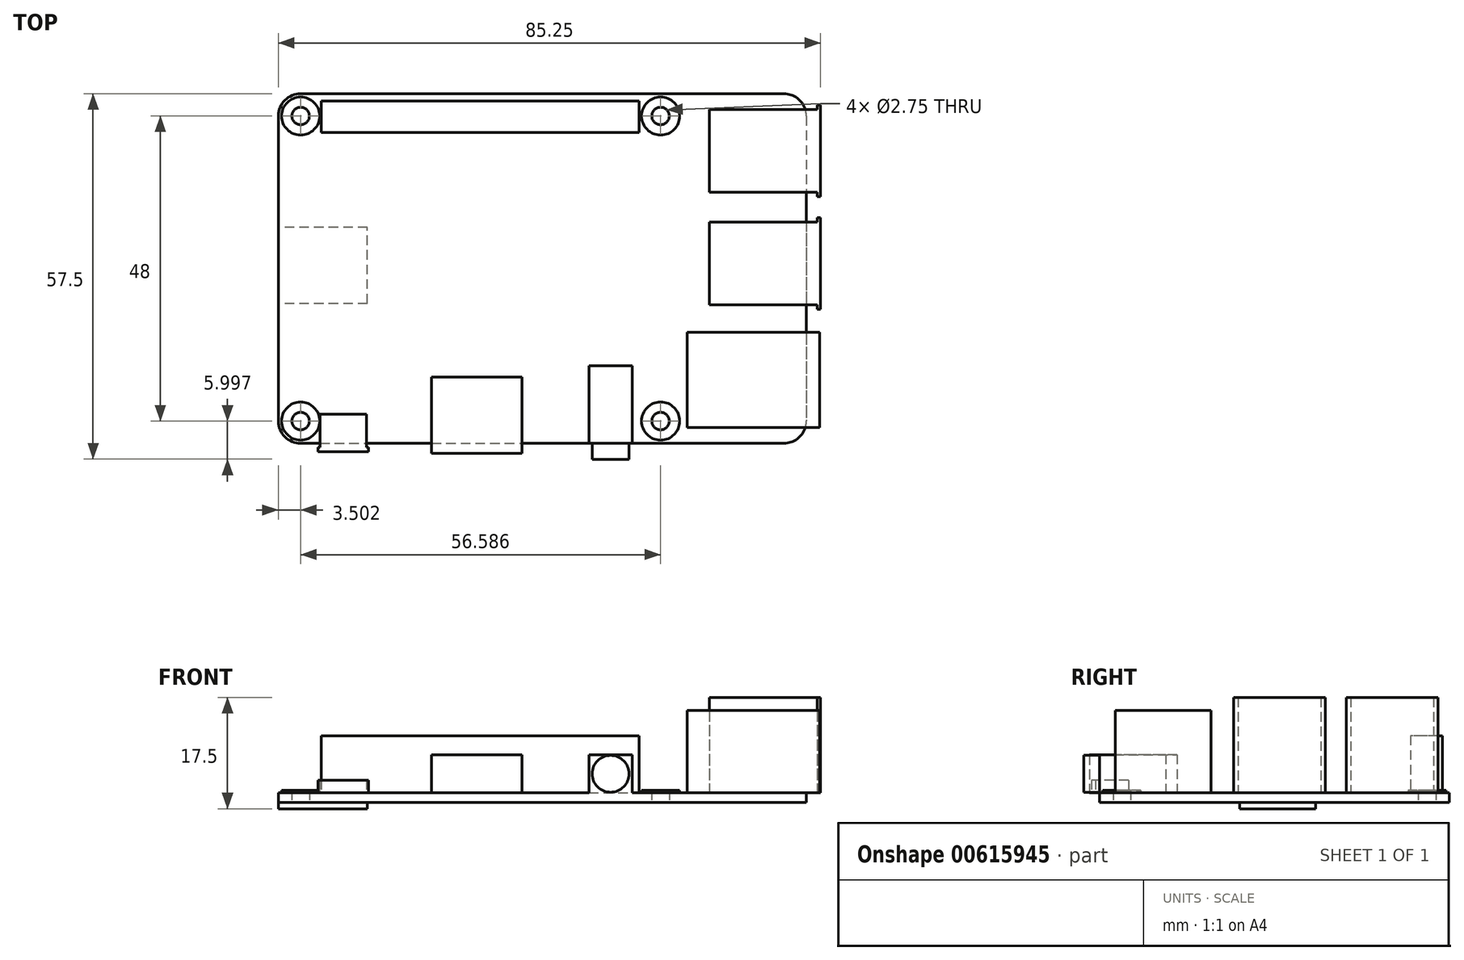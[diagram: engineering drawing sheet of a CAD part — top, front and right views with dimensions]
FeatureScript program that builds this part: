
annotation { "Feature Type Name" : "Feature", "Feature Type Description" : "" }
export const myFeature = defineFeature(function(context is Context, id is Id, definition is map)
    precondition{}
    {
        {
            var Q0;
            Q0=qCreatedBy(makeId("Top.planeOp"),FACE);
            var sketch = newSketch(context, id + "F0", { "sketchPlane" : qUnion([Q0])});
            skLineSegment(sketch, "E0.bottom", {"start": v(20.88, 73.76) * mm, "end": v(96.88, 73.76) * mm});
            skLineSegment(sketch, "E0.top", {"start": v(20.88, 18.76) * mm, "end": v(96.88, 18.76) * mm});
            skLineSegment(sketch, "E0.left", {"start": v(17.38, 70.26) * mm, "end": v(17.38, 22.26) * mm});
            skLineSegment(sketch, "E0.right", {"start": v(100.38, 70.26) * mm, "end": v(100.38, 22.26) * mm});
            skPoint(sketch, "E1.visualSharp", {"position": v(17.38, 73.76) * mm});
            skArc(sketch, "E1.filletArc", {"start": v(20.88, 73.76) * mm, "mid": v(18.4, 72.73) * mm, "end": v(17.38, 70.26) * mm});
            skPoint(sketch, "E2.visualSharp", {"position": v(100.38, 73.76) * mm});
            skArc(sketch, "E2.filletArc", {"start": v(100.38, 70.26) * mm, "mid": v(99.36, 72.73) * mm, "end": v(96.88, 73.76) * mm});
            skPoint(sketch, "E3.visualSharp", {"position": v(100.38, 18.76) * mm});
            skArc(sketch, "E3.filletArc", {"start": v(96.88, 18.76) * mm, "mid": v(99.36, 19.78) * mm, "end": v(100.38, 22.26) * mm});
            skPoint(sketch, "E4.visualSharp", {"position": v(17.38, 18.76) * mm});
            skArc(sketch, "E4.filletArc", {"start": v(17.38, 22.26) * mm, "mid": v(18.4, 19.78) * mm, "end": v(20.88, 18.76) * mm});
            skSolve(sketch);
        }
        {
            var Q0;
            Q0=makeQuery(id+"F0.imprint","IMPRINT",FACE,{"disambiguationData":[TD([[makeQuery(id+"F0.imprint","IMPRINT",EDGE,{"derivedFrom":sQuery(id+"F0.wireOp",EDGE,"E0.bottom")}),-1.0]])]});
            extrude(context, id + "F1", {"entities" : qUnion([Q0]), "depth" : 1.5 * mm, "offsetDistance" : 25 * mm, "symmetric" : true});
        }
        {
            var Q0;
            Q0=makeQuery(id+"F1.opExtrude","CAP_FACE",FACE,{"disambiguationData":[OSD([sQuery(id+"F0.wireOp",EDGE,"E0.bottom"),sQuery(id+"F0.wireOp",EDGE,"E0.top"),sQuery(id+"F0.wireOp",EDGE,"E0.left"),sQuery(id+"F0.wireOp",EDGE,"E0.right"),sQuery(id+"F0.wireOp",EDGE,"E1.filletArc"),sQuery(id+"F0.wireOp",EDGE,"E2.filletArc"),sQuery(id+"F0.wireOp",EDGE,"E3.filletArc"),sQuery(id+"F0.wireOp",EDGE,"E4.filletArc")])],"isStart":false});
            var sketch = newSketch(context, id + "F2", { "sketchPlane" : qUnion([Q0])});
            skLineSegment(sketch, "E5.bottom", {"start": v(85.13, 71.26) * mm, "end": v(102.13, 71.26) * mm});
            skLineSegment(sketch, "E5.top", {"start": v(85.13, 58.26) * mm, "end": v(102.13, 58.26) * mm});
            skLineSegment(sketch, "E5.left", {"start": v(85.13, 71.26) * mm, "end": v(85.13, 58.26) * mm});
            skLineSegment(sketch, "E6", {"start": v(102.13, 71.26) * mm, "end": v(102.13, 71.96) * mm});
            skLineSegment(sketch, "E7", {"start": v(102.13, 71.96) * mm, "end": v(102.63, 71.96) * mm});
            skLineSegment(sketch, "E8", {"start": v(102.13, 58.26) * mm, "end": v(102.13, 57.56) * mm});
            skLineSegment(sketch, "E9", {"start": v(102.13, 57.56) * mm, "end": v(102.63, 57.56) * mm});
            skLineSegment(sketch, "E10", {"start": v(102.63, 57.56) * mm, "end": v(102.63, 71.96) * mm});
            skLineSegment(sketch, "E11.bottom", {"start": v(85.13, 53.55) * mm, "end": v(102.12, 53.55) * mm});
            skLineSegment(sketch, "E11.top", {"start": v(85.13, 40.55) * mm, "end": v(102.13, 40.55) * mm});
            skLineSegment(sketch, "E11.left", {"start": v(85.13, 53.55) * mm, "end": v(85.13, 40.55) * mm});
            skLineSegment(sketch, "E12", {"start": v(102.12, 53.55) * mm, "end": v(102.12, 54.25) * mm});
            skLineSegment(sketch, "E13", {"start": v(102.12, 54.25) * mm, "end": v(102.63, 54.25) * mm});
            skLineSegment(sketch, "E14", {"start": v(102.63, 54.25) * mm, "end": v(102.63, 39.85) * mm});
            skLineSegment(sketch, "E15", {"start": v(102.63, 39.85) * mm, "end": v(102.13, 39.85) * mm});
            skLineSegment(sketch, "E16", {"start": v(102.13, 39.85) * mm, "end": v(102.13, 40.55) * mm});
            skLineSegment(sketch, "E17.bottom", {"start": v(85.13, 36.26) * mm, "end": v(102.5, 36.26) * mm});
            skLineSegment(sketch, "E17.top", {"start": v(85.13, 21.26) * mm, "end": v(102.5, 21.26) * mm});
            skLineSegment(sketch, "E17.right", {"start": v(102.5, 36.26) * mm, "end": v(102.5, 21.26) * mm});
            skLineSegment(sketch, "E18", {"start": v(85.13, 36.26) * mm, "end": v(81.63, 36.26) * mm});
            skLineSegment(sketch, "E19", {"start": v(85.13, 21.26) * mm, "end": v(81.63, 21.26) * mm});
            skLineSegment(sketch, "E20", {"start": v(81.63, 36.26) * mm, "end": v(81.63, 21.26) * mm});
            skSolve(sketch);
        }
        {
            var Q0;
            {var subQ5=sQuery(id+"F2.wireOp",EDGE,"E5.left");Q0=makeQuery(id+"F2.imprint","IMPRINT",FACE,{"disambiguationData":[TD([[makeQuery(id+"F2.imprint","IMPRINT",EDGE,{"derivedFrom":subQ5}),1.0]])]});}
            var Q1;
            {var subQ0=sQuery(id+"F2.wireOp",EDGE,"E6");Q1=makeQuery(id+"F2.imprint","IMPRINT",FACE,{"disambiguationData":[TD([[makeQuery(id+"F2.imprint","IMPRINT",EDGE,{"derivedFrom":subQ0}),-1.0]])]});}
            var Q2;
            {var subQ0=sQuery(id+"F2.wireOp",EDGE,"E12");Q2=makeQuery(id+"F2.imprint","IMPRINT",FACE,{"disambiguationData":[TD([[makeQuery(id+"F2.imprint","IMPRINT",EDGE,{"derivedFrom":subQ0}),-1.0]])]});}
            var Q3;
            {var subQ0=sQuery(id+"F2.wireOp",EDGE,"E11.left");Q3=makeQuery(id+"F2.imprint","IMPRINT",FACE,{"disambiguationData":[TD([[makeQuery(id+"F2.imprint","IMPRINT",EDGE,{"derivedFrom":subQ0}),1.0]])]});}
            var Q4;
            {var subQ4=sQuery(id+"F2.wireOp",EDGE,"E18");Q4=makeQuery(id+"F2.imprint","IMPRINT",FACE,{"disambiguationData":[TD([[makeQuery(id+"F2.imprint","IMPRINT",EDGE,{"derivedFrom":subQ4}),1.0]])]});}
            var Q5;
            {var subQ5=sQuery(id+"F2.wireOp",EDGE,"E17.right");Q5=makeQuery(id+"F2.imprint","IMPRINT",FACE,{"disambiguationData":[TD([[makeQuery(id+"F2.imprint","IMPRINT",EDGE,{"derivedFrom":subQ5}),-1.0]])]});}
            extrude(context, id + "F3", {"entities" : qUnion([Q0, Q1, Q2, Q3, Q4, Q5]), "operationType" : NewBodyOperationType.ADD, "depth" : 15 * mm, "offsetDistance" : 25 * mm});
        }
        {
            var Q0;
            Q0=makeQuery(id+"F3.opExtrude","CAP_FACE",FACE,{"disambiguationData":[OSD([sQuery(id+"F2.wireOp",EDGE,"E17.bottom"),sQuery(id+"F2.wireOp",EDGE,"E17.top"),sQuery(id+"F2.wireOp",EDGE,"E17.right"),sQuery(id+"F2.wireOp",EDGE,"E18"),sQuery(id+"F2.wireOp",EDGE,"E19"),sQuery(id+"F2.wireOp",EDGE,"E20")])],"isStart":false});
            extrude(context, id + "F4", {"entities" : qUnion([Q0]), "operationType" : NewBodyOperationType.REMOVE, "oppositeDirection" : true, "depth" : 2 * mm, "offsetDistance" : 25 * mm});
        }
        {
            var Q0;
            Q0=makeQuery(id+"F1.opExtrude","CAP_FACE",FACE,{"disambiguationData":[OSD([sQuery(id+"F0.wireOp",EDGE,"E0.bottom"),sQuery(id+"F0.wireOp",EDGE,"E0.top"),sQuery(id+"F0.wireOp",EDGE,"E0.left"),sQuery(id+"F0.wireOp",EDGE,"E0.right"),sQuery(id+"F0.wireOp",EDGE,"E1.filletArc"),sQuery(id+"F0.wireOp",EDGE,"E2.filletArc"),sQuery(id+"F0.wireOp",EDGE,"E3.filletArc"),sQuery(id+"F0.wireOp",EDGE,"E4.filletArc")])],"isStart":false});
            var sketch = newSketch(context, id + "F5", { "sketchPlane" : qUnion([Q0])});
            skLineSegment(sketch, "E21.bottom", {"start": v(24.1, 72.64) * mm, "end": v(74.1, 72.64) * mm});
            skLineSegment(sketch, "E21.top", {"start": v(24.1, 67.64) * mm, "end": v(74.1, 67.64) * mm});
            skLineSegment(sketch, "E21.left", {"start": v(24.1, 72.64) * mm, "end": v(24.1, 67.64) * mm});
            skLineSegment(sketch, "E21.right", {"start": v(74.1, 72.64) * mm, "end": v(74.1, 67.64) * mm});
            skSolve(sketch);
        }
        {
            var Q0;
            Q0=makeQuery(id+"F5.imprint","IMPRINT",FACE,{"disambiguationData":[TD([[makeQuery(id+"F5.imprint","IMPRINT",EDGE,{"derivedFrom":sQuery(id+"F5.wireOp",EDGE,"E21.bottom")}),-1.0]])]});
            extrude(context, id + "F6", {"entities" : qUnion([Q0]), "operationType" : NewBodyOperationType.ADD, "depth" : 9 * mm, "offsetDistance" : 25 * mm});
        }
        {
            var Q0;
            Q0=makeQuery(id+"F1.opExtrude","CAP_FACE",FACE,{"disambiguationData":[OSD([sQuery(id+"F0.wireOp",EDGE,"E0.bottom"),sQuery(id+"F0.wireOp",EDGE,"E0.top"),sQuery(id+"F0.wireOp",EDGE,"E0.left"),sQuery(id+"F0.wireOp",EDGE,"E0.right"),sQuery(id+"F0.wireOp",EDGE,"E1.filletArc"),sQuery(id+"F0.wireOp",EDGE,"E2.filletArc"),sQuery(id+"F0.wireOp",EDGE,"E3.filletArc"),sQuery(id+"F0.wireOp",EDGE,"E4.filletArc")])],"isStart":false});
            var sketch = newSketch(context, id + "F7", { "sketchPlane" : qUnion([Q0])});
            skLineSegment(sketch, "E22", {"start": v(23.93, 23.31) * mm, "end": v(31.23, 23.31) * mm});
            skLineSegment(sketch, "E23", {"start": v(23.93, 23.31) * mm, "end": v(23.93, 18.11) * mm});
            skLineSegment(sketch, "E24", {"start": v(31.23, 23.31) * mm, "end": v(31.23, 18.11) * mm});
            skLineSegment(sketch, "E25", {"start": v(31.23, 18.11) * mm, "end": v(31.53, 18.11) * mm});
            skLineSegment(sketch, "E26", {"start": v(31.53, 18.11) * mm, "end": v(31.53, 17.46) * mm});
            skLineSegment(sketch, "E27", {"start": v(23.93, 18.11) * mm, "end": v(23.63, 18.11) * mm});
            skLineSegment(sketch, "E28", {"start": v(23.63, 18.11) * mm, "end": v(23.63, 17.46) * mm});
            skLineSegment(sketch, "E29", {"start": v(23.63, 17.46) * mm, "end": v(31.53, 17.46) * mm});
            skLineSegment(sketch, "E30", {"start": v(41.47, 29.17) * mm, "end": v(55.67, 29.17) * mm});
            skLineSegment(sketch, "E31", {"start": v(41.47, 29.17) * mm, "end": v(41.47, 17.17) * mm});
            skLineSegment(sketch, "E32", {"start": v(41.47, 17.17) * mm, "end": v(55.67, 17.17) * mm});
            skLineSegment(sketch, "E33", {"start": v(55.67, 17.17) * mm, "end": v(55.67, 29.17) * mm});
            skLineSegment(sketch, "E34", {"start": v(66.21, 18.76) * mm, "end": v(66.21, 30.96) * mm});
            skLineSegment(sketch, "E35", {"start": v(66.21, 30.96) * mm, "end": v(73.01, 30.96) * mm});
            skLineSegment(sketch, "E36", {"start": v(73.01, 30.96) * mm, "end": v(73.01, 18.76) * mm});
            skSolve(sketch);
        }
        {
            var Q0;
            {var subQ0=sQuery(id+"F7.wireOp",EDGE,"E22");Q0=makeQuery(id+"F7.imprint","IMPRINT",FACE,{"disambiguationData":[TD([[makeQuery(id+"F7.imprint","IMPRINT",EDGE,{"derivedFrom":subQ0}),-1.0]])]});}
            var Q1;
            {var subQ0=sQuery(id+"F7.wireOp",EDGE,"E25");Q1=makeQuery(id+"F7.imprint","IMPRINT",FACE,{"disambiguationData":[TD([[makeQuery(id+"F7.imprint","IMPRINT",EDGE,{"derivedFrom":subQ0}),-1.0]])]});}
            var Q2;
            {var subQ0=sQuery(id+"F7.wireOp",EDGE,"E30");Q2=makeQuery(id+"F7.imprint","IMPRINT",FACE,{"disambiguationData":[TD([[makeQuery(id+"F7.imprint","IMPRINT",EDGE,{"derivedFrom":subQ0}),-1.0]])]});}
            var Q3;
            {var subQ0=sQuery(id+"F7.wireOp",EDGE,"E34");Q3=makeQuery(id+"F7.imprint","IMPRINT",FACE,{"disambiguationData":[TD([[makeQuery(id+"F7.imprint","IMPRINT",EDGE,{"derivedFrom":subQ0}),-1.0]])]});}
            var Q4;
            {var subQ0=sQuery(id+"F7.wireOp",EDGE,"E32");Q4=makeQuery(id+"F7.imprint","IMPRINT",FACE,{"disambiguationData":[TD([[makeQuery(id+"F7.imprint","IMPRINT",EDGE,{"derivedFrom":subQ0}),1.0]])]});}
            extrude(context, id + "F8", {"entities" : qUnion([Q0, Q1, Q2, Q3, Q4]), "operationType" : NewBodyOperationType.ADD, "depth" : 6 * mm, "offsetDistance" : 25 * mm});
        }
        {
            var Q0;
            Q0=makeQuery(id+"F8.opExtrude","CAP_FACE",FACE,{"disambiguationData":[OSD([sQuery(id+"F7.wireOp",EDGE,"E22"),sQuery(id+"F7.wireOp",EDGE,"E23"),sQuery(id+"F7.wireOp",EDGE,"E24"),sQuery(id+"F7.wireOp",EDGE,"E25"),sQuery(id+"F7.wireOp",EDGE,"E26"),sQuery(id+"F7.wireOp",EDGE,"E27"),sQuery(id+"F7.wireOp",EDGE,"E28"),sQuery(id+"F7.wireOp",EDGE,"E29")])],"isStart":false});
            extrude(context, id + "F9", {"entities" : qUnion([Q0]), "operationType" : NewBodyOperationType.REMOVE, "oppositeDirection" : true, "depth" : 4 * mm, "offsetDistance" : 25 * mm});
        }
        {
            var Q0;
            Q0=makeQuery(id+"F1.opExtrude","CAP_FACE",FACE,{"disambiguationData":[OSD([sQuery(id+"F0.wireOp",EDGE,"E0.bottom"),sQuery(id+"F0.wireOp",EDGE,"E0.top"),sQuery(id+"F0.wireOp",EDGE,"E0.left"),sQuery(id+"F0.wireOp",EDGE,"E0.right"),sQuery(id+"F0.wireOp",EDGE,"E1.filletArc"),sQuery(id+"F0.wireOp",EDGE,"E2.filletArc"),sQuery(id+"F0.wireOp",EDGE,"E3.filletArc"),sQuery(id+"F0.wireOp",EDGE,"E4.filletArc")])],"isStart":true});
            var sketch = newSketch(context, id + "F10", { "sketchPlane" : qUnion([Q0])});
            skLineSegment(sketch, "E37", {"start": v(31.38, -40.76) * mm, "end": v(31.38, -52.76) * mm});
            skLineSegment(sketch, "E38", {"start": v(31.38, -52.76) * mm, "end": v(17.38, -52.76) * mm});
            skPoint(sketch, "E39.start.orphan", {"position": v(19.9, -40.76) * mm});
            skLineSegment(sketch, "E40", {"start": v(31.38, -40.76) * mm, "end": v(17.38, -40.76) * mm});
            skSolve(sketch);
        }
        {
            var Q0;
            Q0=makeQuery(id+"F10.imprint","IMPRINT",FACE,{"disambiguationData":[TD([[makeQuery(id+"F10.imprint","IMPRINT",EDGE,{"derivedFrom":sQuery(id+"F10.wireOp",EDGE,"E37")}),-1.0]])]});
            extrude(context, id + "F11", {"entities" : qUnion([Q0]), "operationType" : NewBodyOperationType.ADD, "depth" : 1 * mm, "offsetDistance" : 25 * mm});
        }
        {
            var Q0;
            {var subQ0=sQuery(id+"F0.wireOp",EDGE,"E0.top");Q0=makeQuery(id+"F8.boolean.opBoolean","MERGE",FACE,{"derivedFrom":[makeQuery(id+"F1.opExtrude","SWEPT_FACE",FACE,{"disambiguationData":[OSD([subQ0])]}),makeQuery(id+"F8.opExtrude","SWEPT_FACE",FACE,{"disambiguationData":[OSD([subQ0])]})]});}
            var sketch = newSketch(context, id + "F12", { "sketchPlane" : qUnion([Q0])});
            skCircle(sketch, "E41", {"center": v(69.61, 3.75) * mm, "radius": 2.9 * mm});
            skPoint(sketch, "E41.centerSnap0", {"position": v(66.21, 3.75) * mm});
            skPoint(sketch, "E42.start.orphan", {"position": v(69.61, 6.75) * mm});
            skSolve(sketch);
        }
        {
            var Q0;
            Q0=makeQuery(id+"F12.imprint","IMPRINT",FACE,{"disambiguationData":[TD([[makeQuery(id+"F12.imprint","IMPRINT",EDGE,{"derivedFrom":sQuery(id+"F12.wireOp",EDGE,"E41")}),1.0]])]});
            extrude(context, id + "F13", {"entities" : qUnion([Q0]), "operationType" : NewBodyOperationType.ADD, "depth" : 2.5 * mm, "offsetDistance" : 25 * mm});
        }
        {
            var Q0;
            Q0=makeQuery(id+"F1.opExtrude","CAP_FACE",FACE,{"disambiguationData":[OSD([sQuery(id+"F0.wireOp",EDGE,"E0.bottom"),sQuery(id+"F0.wireOp",EDGE,"E0.top"),sQuery(id+"F0.wireOp",EDGE,"E0.left"),sQuery(id+"F0.wireOp",EDGE,"E0.right"),sQuery(id+"F0.wireOp",EDGE,"E1.filletArc"),sQuery(id+"F0.wireOp",EDGE,"E2.filletArc"),sQuery(id+"F0.wireOp",EDGE,"E3.filletArc"),sQuery(id+"F0.wireOp",EDGE,"E4.filletArc")])],"isStart":false});
            var sketch = newSketch(context, id + "F14", { "sketchPlane" : qUnion([Q0])});
            skCircle(sketch, "E43", {"center": v(20.88, 70.26) * mm, "radius": 3 * mm});
            skCircle(sketch, "E44", {"center": v(20.88, 70.26) * mm, "radius": 1.38 * mm});
            skCircle(sketch, "E45", {"center": v(20.88, 22.26) * mm, "radius": 3 * mm});
            skCircle(sketch, "E46", {"center": v(20.88, 22.26) * mm, "radius": 1.38 * mm});
            skCircle(sketch, "E47", {"center": v(77.47, 70.26) * mm, "radius": 3 * mm});
            skCircle(sketch, "E48", {"center": v(77.47, 70.26) * mm, "radius": 1.38 * mm});
            skCircle(sketch, "E49", {"center": v(77.47, 22.26) * mm, "radius": 3 * mm});
            skCircle(sketch, "E50", {"center": v(77.47, 22.26) * mm, "radius": 1.38 * mm});
            skSolve(sketch);
        }
        {
            var Q0;
            Q0=makeQuery(id+"F14.imprint","IMPRINT",FACE,{"disambiguationData":[TD([[makeQuery(id+"F14.imprint","IMPRINT",EDGE,{"derivedFrom":sQuery(id+"F14.wireOp",EDGE,"E47")}),1.0]])]});
            var Q1;
            Q1=makeQuery(id+"F14.imprint","IMPRINT",FACE,{"disambiguationData":[TD([[makeQuery(id+"F14.imprint","IMPRINT",EDGE,{"derivedFrom":sQuery(id+"F14.wireOp",EDGE,"E43")}),1.0]])]});
            var Q2;
            Q2=makeQuery(id+"F14.imprint","IMPRINT",FACE,{"disambiguationData":[TD([[makeQuery(id+"F14.imprint","IMPRINT",EDGE,{"derivedFrom":sQuery(id+"F14.wireOp",EDGE,"E45")}),1.0]])]});
            var Q3;
            Q3=makeQuery(id+"F14.imprint","IMPRINT",FACE,{"disambiguationData":[TD([[makeQuery(id+"F14.imprint","IMPRINT",EDGE,{"derivedFrom":sQuery(id+"F14.wireOp",EDGE,"E49")}),1.0]])]});
            extrude(context, id + "F15", {"entities" : qUnion([Q0, Q1, Q2, Q3]), "operationType" : NewBodyOperationType.ADD, "depth" : 0.4 * mm, "offsetDistance" : 25 * mm});
        }
        {
            var Q0;
            Q0=makeQuery(id+"F15.boolean.opBoolean","SPLIT",FACE,{"disambiguationData":[TD([makeQuery(id+"F15.opExtrude","SWEPT_FACE",FACE,{"disambiguationData":[OSD([sQuery(id+"F14.wireOp",EDGE,"E48")])]})])],"derivedFrom":makeQuery(id+"F1.opExtrude","CAP_FACE",FACE,{"disambiguationData":[OSD([sQuery(id+"F0.wireOp",EDGE,"E0.bottom"),sQuery(id+"F0.wireOp",EDGE,"E0.top"),sQuery(id+"F0.wireOp",EDGE,"E0.left"),sQuery(id+"F0.wireOp",EDGE,"E0.right"),sQuery(id+"F0.wireOp",EDGE,"E1.filletArc"),sQuery(id+"F0.wireOp",EDGE,"E2.filletArc"),sQuery(id+"F0.wireOp",EDGE,"E3.filletArc"),sQuery(id+"F0.wireOp",EDGE,"E4.filletArc")])],"isStart":false})});
            var Q1;
            Q1=makeQuery(id+"F15.boolean.opBoolean","SPLIT",FACE,{"disambiguationData":[TD([makeQuery(id+"F15.opExtrude","SWEPT_FACE",FACE,{"disambiguationData":[OSD([sQuery(id+"F14.wireOp",EDGE,"E50")])]})])],"derivedFrom":makeQuery(id+"F1.opExtrude","CAP_FACE",FACE,{"disambiguationData":[OSD([sQuery(id+"F0.wireOp",EDGE,"E0.bottom"),sQuery(id+"F0.wireOp",EDGE,"E0.top"),sQuery(id+"F0.wireOp",EDGE,"E0.left"),sQuery(id+"F0.wireOp",EDGE,"E0.right"),sQuery(id+"F0.wireOp",EDGE,"E1.filletArc"),sQuery(id+"F0.wireOp",EDGE,"E2.filletArc"),sQuery(id+"F0.wireOp",EDGE,"E3.filletArc"),sQuery(id+"F0.wireOp",EDGE,"E4.filletArc")])],"isStart":false})});
            var Q2;
            Q2=makeQuery(id+"F15.boolean.opBoolean","SPLIT",FACE,{"disambiguationData":[TD([makeQuery(id+"F15.opExtrude","SWEPT_FACE",FACE,{"disambiguationData":[OSD([sQuery(id+"F14.wireOp",EDGE,"E46")])]})])],"derivedFrom":makeQuery(id+"F1.opExtrude","CAP_FACE",FACE,{"disambiguationData":[OSD([sQuery(id+"F0.wireOp",EDGE,"E0.bottom"),sQuery(id+"F0.wireOp",EDGE,"E0.top"),sQuery(id+"F0.wireOp",EDGE,"E0.left"),sQuery(id+"F0.wireOp",EDGE,"E0.right"),sQuery(id+"F0.wireOp",EDGE,"E1.filletArc"),sQuery(id+"F0.wireOp",EDGE,"E2.filletArc"),sQuery(id+"F0.wireOp",EDGE,"E3.filletArc"),sQuery(id+"F0.wireOp",EDGE,"E4.filletArc")])],"isStart":false})});
            var Q3;
            Q3=makeQuery(id+"F15.boolean.opBoolean","SPLIT",FACE,{"disambiguationData":[TD([makeQuery(id+"F15.opExtrude","SWEPT_FACE",FACE,{"disambiguationData":[OSD([sQuery(id+"F14.wireOp",EDGE,"E44")])]})])],"derivedFrom":makeQuery(id+"F1.opExtrude","CAP_FACE",FACE,{"disambiguationData":[OSD([sQuery(id+"F0.wireOp",EDGE,"E0.bottom"),sQuery(id+"F0.wireOp",EDGE,"E0.top"),sQuery(id+"F0.wireOp",EDGE,"E0.left"),sQuery(id+"F0.wireOp",EDGE,"E0.right"),sQuery(id+"F0.wireOp",EDGE,"E1.filletArc"),sQuery(id+"F0.wireOp",EDGE,"E2.filletArc"),sQuery(id+"F0.wireOp",EDGE,"E3.filletArc"),sQuery(id+"F0.wireOp",EDGE,"E4.filletArc")])],"isStart":false})});
            extrude(context, id + "F16", {"entities" : qUnion([Q0, Q1, Q2, Q3]), "operationType" : NewBodyOperationType.REMOVE, "oppositeDirection" : true, "depth" : 25 * mm, "offsetDistance" : 25 * mm});
        }
    });
